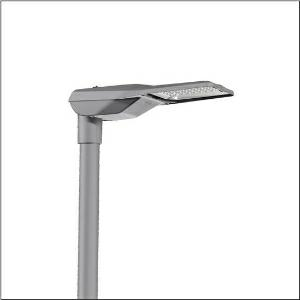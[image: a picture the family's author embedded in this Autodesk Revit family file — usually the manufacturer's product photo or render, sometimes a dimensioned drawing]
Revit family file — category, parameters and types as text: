
# Revit family: streetlight_sl_21_mini___st0_8a_5xe2c33s08hb_71fe
name_source: partatom
category: Lighting Fixtures
units: mm (PartAtom-declared; Revit-internal decimal feet)

## family parameters
Cut with Voids When Loaded = No
Host = Face
Light Source = No
Part Type = Normal
Room Calculation Point = No
Round Connector Dimension = Use Diameter
Shared = No

## types (1)
- --- (1 x LED, 9040 lm, 66 W, 3000K)
    Apparent Load = 66 VA
    CIE Flux Codes = 38 75 97 100 100
    Color Rendering = 70
    Color Temperature = 3000K
    Default Elevation = 1800 mm
    Description = Streetlight SL 21 mini, mast luminaire, primary light control with lens, of PMMA, primary optical cover: cover, of toughened safety glass, transparent, light distribution: ST0.8a, light emission: direct distribution, primary light characteristic: asymmetric, installation type: side-entry, post-top, LED, High Power LED, rated luminous flux: 9.040lm, luminous efficacy: 137lm/W, light colour: 730, colour temperature: 3000K, control gear: D4i, control: overheat protection, constant luminous flux control, time-dependent luminous flux control, flexible luminous flux parameterisation, pre-setting: logarithmic dimming characteristic, mains connection: 220..240V, AC, 50/60Hz, start of lifetime: 66W, end of service life: 69W, reduction: 30W, luminaire housing, of diecast aluminium, powder-coated, SITECO metallic grey (DB 702S), corrosivity category C5 high according to DIN EN ISO 12944, please order mast flange separately, inclination adjustable: 0°, 5°, 10°, 15°, sealing non-destructively replaceable, multi-level sealing system, length: 628mm, width: 235mm, height: 110mm, mast flange for spigot size: 42mm (side-entry): 5XC10008XM4, 60/48mm (side-entry/post-top): 5XC10108XM2, 76/60mm (side-entry/post-top): 5XC10108XM1, mounting height: 4..8m, Smart Interface above, protection rating (complete): IP66, insulation class (complete): insulation class II (safety insulation), certification: CE, ENEC, ENEC+, VDE, impact resistance: IK10, permissible operating ambient temperature for outdoor applications: -40..+50°C, standard-compliant lighting for roads and squares, packaging unit: 1 piece

Light Distribution: ST0.8a
    Height = 110 mm
    Lamp = 1 x LED
    Lamp Light Flux = 9040 lm
    Lamp Power = 66 W
    Lamp count = 1
    Length = 625 mm
    Luminous efficacy = 137 lm/W
    Manufacturer = Siteco
    ModVariant = No
    Model = 5XE2C33S08HB
    Number of Poles = 1
    OnlyDefault = Yes
    Power Factor = 1
    Product Name = Streetlight SL 21 mini | ST0.8a
    Product group = mast luminaire | pylon top
    ProductGroupID = 6100
    Protection Class = Protection class II
    Protection Degree = IP 66
    RLX_Detail_Level = 1
    RLX_Emergency_Light_Flux = 0 lm
    RLX_Emergency_Type = 0
    RLX_Emergency_Type_DB = No
    RlxData = <blob elided: 26193 chars, md5=bba69987>
    Socket = socket
    Standby Power = 0 W
    System Light Flux = 9040 lm
    System Power = 66 W
    Type Comments = factory setting: luminous flux: 100 % | dim-lin: 254 | 670 mA
    Type Image = l_1003515.jpg
    URL = http://relux.com
    VarID = @adj_182955
    Voltage = 0 V
    Weight = 0.00 kg
    Width = 234 mm

## geometry (parser evidence)
native form markers: Blend x4, Sweep x10
no freeform markers — native parametric forms only
